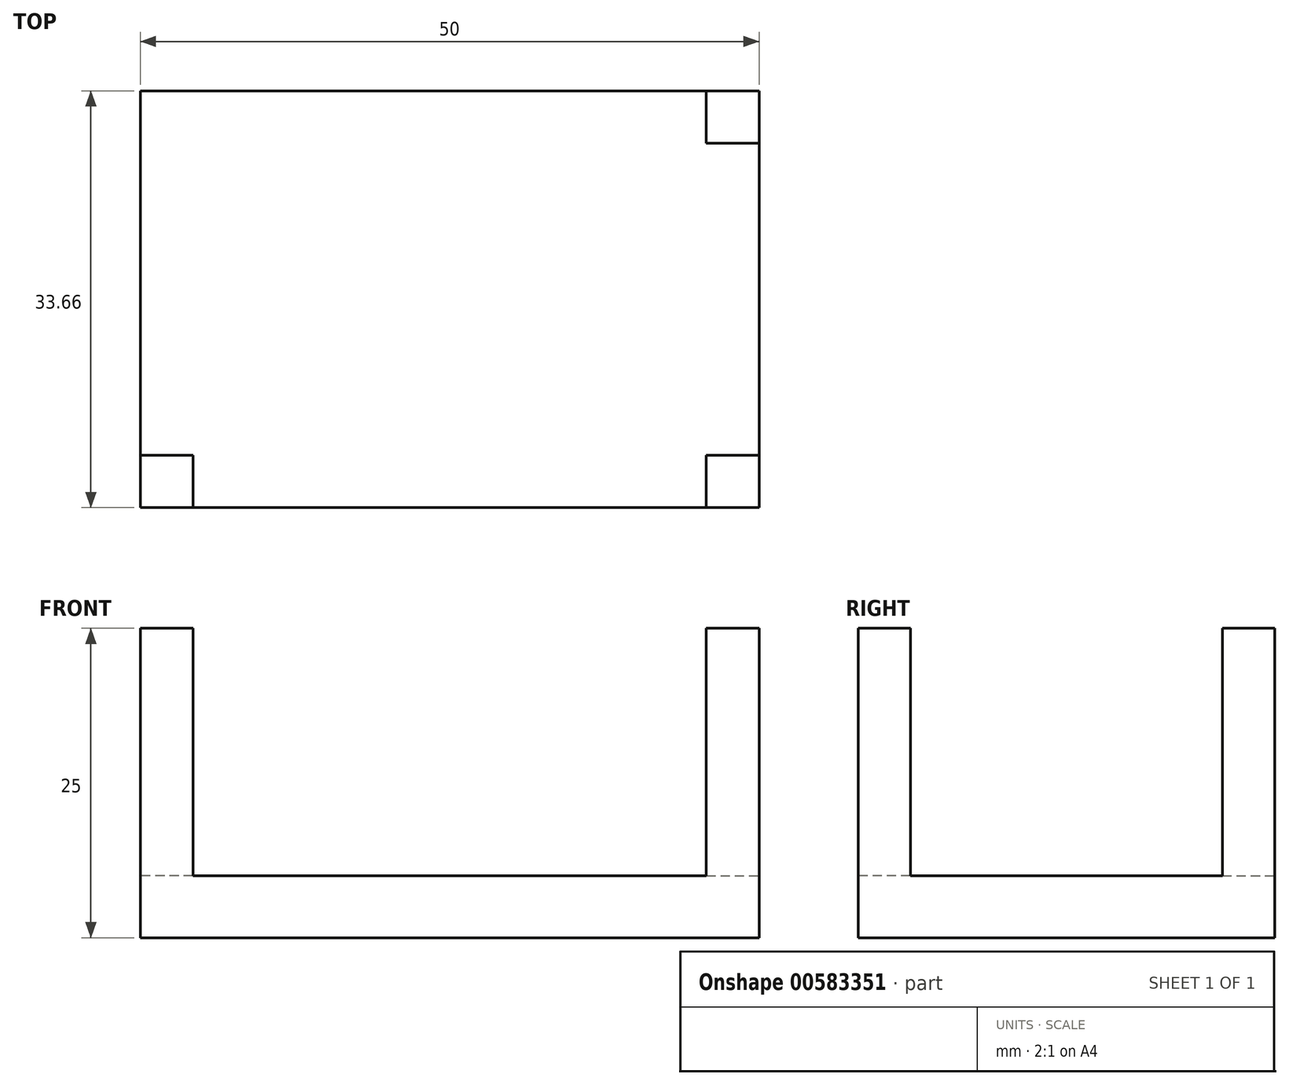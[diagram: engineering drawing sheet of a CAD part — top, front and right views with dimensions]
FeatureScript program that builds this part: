
annotation { "Feature Type Name" : "Feature", "Feature Type Description" : "" }
export const myFeature = defineFeature(function(context is Context, id is Id, definition is map)
    precondition{}
    {
        {
            var Q0;
            Q0=qCreatedBy(makeId("Top.planeOp"),FACE);
            var sketch = newSketch(context, id + "F0", { "sketchPlane" : qUnion([Q0])});
            skLineSegment(sketch, "E0.bottom", {"start": v(-25, 16.83) * mm, "end": v(25, 16.83) * mm});
            skLineSegment(sketch, "E0.top", {"start": v(-25, -16.83) * mm, "end": v(25, -16.83) * mm});
            skLineSegment(sketch, "E0.left", {"start": v(-25, 16.83) * mm, "end": v(-25, -16.83) * mm});
            skLineSegment(sketch, "E0.right", {"start": v(25, 16.83) * mm, "end": v(25, -16.83) * mm});
            skPoint(sketch, "E0.middle", {"position": v(0, 0) * mm});
            skLineSegment(sketch, "E1.bottom", {"start": v(-25, 16.83) * mm, "end": v(-20.74, 16.83) * mm});
            skLineSegment(sketch, "E1.top", {"start": v(-25, 12.6) * mm, "end": v(-20.74, 12.6) * mm});
            skLineSegment(sketch, "E1.left", {"start": v(-25, 16.83) * mm, "end": v(-25, 12.6) * mm});
            skLineSegment(sketch, "E1.right", {"start": v(-20.74, 16.83) * mm, "end": v(-20.74, 12.6) * mm});
            skLineSegment(sketch, "E2.MirrorCS", {"start": v(-25, -12.6) * mm, "end": v(-20.74, -12.6) * mm});
            skLineSegment(sketch, "E3.MirrorCS", {"start": v(-20.74, -16.83) * mm, "end": v(-20.74, -12.6) * mm});
            skLineSegment(sketch, "E4.MirrorCS", {"start": v(-25, -16.83) * mm, "end": v(-20.74, -16.83) * mm});
            skLineSegment(sketch, "E5.MirrorCS", {"start": v(-25, -16.83) * mm, "end": v(-25, -12.6) * mm});
            skLineSegment(sketch, "E6.MirrorCS", {"start": v(20.74, 16.83) * mm, "end": v(20.74, 12.6) * mm});
            skLineSegment(sketch, "E7.MirrorCS", {"start": v(25, 16.83) * mm, "end": v(20.74, 16.83) * mm});
            skLineSegment(sketch, "E8.MirrorCS", {"start": v(25, 16.83) * mm, "end": v(25, 12.6) * mm});
            skLineSegment(sketch, "E9.MirrorCS", {"start": v(25, 12.6) * mm, "end": v(20.74, 12.6) * mm});
            skLineSegment(sketch, "E10.MirrorCS", {"start": v(25, -12.6) * mm, "end": v(20.74, -12.6) * mm});
            skLineSegment(sketch, "E11.MirrorCS", {"start": v(25, -16.83) * mm, "end": v(25, -12.6) * mm});
            skLineSegment(sketch, "E12.MirrorCS", {"start": v(25, -16.83) * mm, "end": v(20.74, -16.83) * mm});
            skLineSegment(sketch, "E13.MirrorCS", {"start": v(20.74, -16.83) * mm, "end": v(20.74, -12.6) * mm});
            skSolve(sketch);
        }
        {
            var Q0;
            Q0 = qSketchRegion(id + "F0", true);
            extrude(context, id + "F1", {"entities" : qUnion([Q0]), "depth" : 5 * mm, "offsetDistance" : 25 * mm});
        }
        {
            var Q0;
            Q0=makeQuery(id+"F0.imprint","IMPRINT",FACE,{"disambiguationData":[TD([[makeQuery(id+"F0.imprint","IMPRINT",EDGE,{"derivedFrom":sQuery(id+"F0.wireOp",EDGE,"E6.MirrorCS")}),1.0]])]});
            var Q1;
            Q1=makeQuery(id+"F0.imprint","IMPRINT",FACE,{"disambiguationData":[TD([[makeQuery(id+"F0.imprint","IMPRINT",EDGE,{"derivedFrom":sQuery(id+"F0.wireOp",EDGE,"E10.MirrorCS")}),1.0]])]});
            var Q2;
            Q2=makeQuery(id+"F0.imprint","IMPRINT",FACE,{"disambiguationData":[TD([[makeQuery(id+"F0.imprint","IMPRINT",EDGE,{"derivedFrom":sQuery(id+"F0.wireOp",EDGE,"E2.MirrorCS")}),-1.0]])]});
            var Q3;
            Q3=makeQuery(id+"F0.imprint","IMPRINT",FACE,{"disambiguationData":[TD([[makeQuery(id+"F0.imprint","IMPRINT",EDGE,{"derivedFrom":sQuery(id+"F0.wireOp",EDGE,"E1.bottom")}),-1.0]])]});
            extrude(context, id + "F2", {"entities" : qUnion([Q0, Q1, Q2, Q3]), "operationType" : NewBodyOperationType.ADD, "depth" : 25 * mm, "offsetDistance" : 25 * mm});
        }
    });
